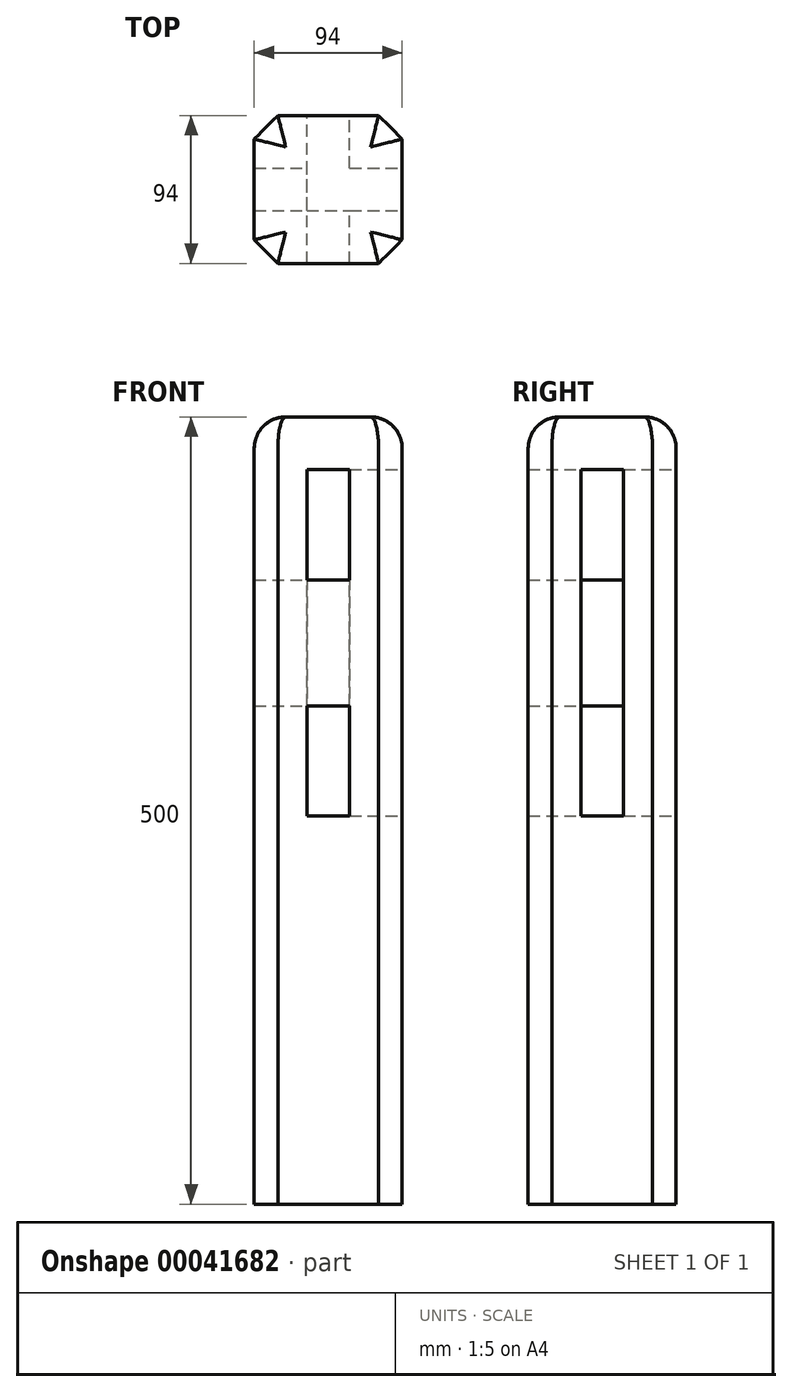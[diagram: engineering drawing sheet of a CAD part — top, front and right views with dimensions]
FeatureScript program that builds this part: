
annotation { "Feature Type Name" : "Feature", "Feature Type Description" : "" }
export const myFeature = defineFeature(function(context is Context, id is Id, definition is map)
    precondition{}
    {
        {
            var Q0;
            Q0=qCreatedBy(makeId("Top.planeOp"),FACE);
            var sketch = newSketch(context, id + "F0", { "sketchPlane" : qUnion([Q0])});
            skLineSegment(sketch, "E0.bottom", {"start": v(-47.13, 48) * mm, "end": v(46.87, 48) * mm});
            skLineSegment(sketch, "E0.top", {"start": v(-47.13, -46) * mm, "end": v(46.87, -46) * mm});
            skLineSegment(sketch, "E0.left", {"start": v(-47.13, 48) * mm, "end": v(-47.13, -46) * mm});
            skLineSegment(sketch, "E0.right", {"start": v(46.87, 48) * mm, "end": v(46.87, -46) * mm});
            skSolve(sketch);
        }
        {
            var Q0;
            Q0=makeQuery(id+"F0.imprint","IMPRINT",FACE,{"disambiguationData":[TD([[makeQuery(id+"F0.imprint","IMPRINT",EDGE,{"derivedFrom":sQuery(id+"F0.wireOp",EDGE,"E0.bottom")}),-1.0]])]});
            extrude(context, id + "F1", {"entities" : qUnion([Q0]), "depth" : 500 * mm});
        }
        {
            var Q0;
            Q0=makeQuery(id+"F1.opExtrude","SWEPT_FACE",FACE,{"disambiguationData":[OSD([sQuery(id+"F0.wireOp",EDGE,"E0.top")])]});
            var sketch = newSketch(context, id + "F2", { "sketchPlane" : qUnion([Q0])});
            skLineSegment(sketch, "E1.bottom", {"start": v(-13.63, 466.5) * mm, "end": v(13.37, 466.5) * mm});
            skLineSegment(sketch, "E1.top", {"start": v(-13.63, 246.5) * mm, "end": v(13.37, 246.5) * mm});
            skLineSegment(sketch, "E1.left", {"start": v(-13.63, 466.5) * mm, "end": v(-13.63, 246.5) * mm});
            skLineSegment(sketch, "E1.right", {"start": v(13.37, 466.5) * mm, "end": v(13.37, 246.5) * mm});
            skLineSegment(sketch, "E2.bottom", {"start": v(-13.63, 396.5) * mm, "end": v(13.37, 396.5) * mm});
            skLineSegment(sketch, "E2.top", {"start": v(-13.63, 316.5) * mm, "end": v(13.37, 316.5) * mm});
            skLineSegment(sketch, "E2.left", {"start": v(-13.63, 396.5) * mm, "end": v(-13.63, 316.5) * mm});
            skLineSegment(sketch, "E2.right", {"start": v(13.37, 396.5) * mm, "end": v(13.37, 316.5) * mm});
            skSolve(sketch);
        }
        {
            var Q0;
            Q0=qSketchRegion(id+"F2",true);
            extrude(context, id + "F3", {"entities" : qUnion([Q0]), "operationType" : NewBodyOperationType.REMOVE, "oppositeDirection" : true, "depth" : 60.5 * mm});
        }
        {
            var Q0;
            Q0=makeQuery(id+"F1.opExtrude","SWEPT_FACE",FACE,{"disambiguationData":[OSD([sQuery(id+"F0.wireOp",EDGE,"E0.right")])]});
            var sketch = newSketch(context, id + "F4", { "sketchPlane" : qUnion([Q0])});
            skLineSegment(sketch, "E3.bottom", {"start": v(-12.5, 466.5) * mm, "end": v(14.5, 466.5) * mm});
            skLineSegment(sketch, "E3.top", {"start": v(-12.5, 246.5) * mm, "end": v(14.5, 246.5) * mm});
            skLineSegment(sketch, "E3.left", {"start": v(-12.5, 466.5) * mm, "end": v(-12.5, 246.5) * mm});
            skLineSegment(sketch, "E3.right", {"start": v(14.5, 466.5) * mm, "end": v(14.5, 246.5) * mm});
            skSolve(sketch);
        }
        {
            var Q0;
            Q0=makeQuery(id+"F4.imprint","IMPRINT",FACE,{"disambiguationData":[TD([[makeQuery(id+"F4.imprint","IMPRINT",EDGE,{"derivedFrom":sQuery(id+"F4.wireOp",EDGE,"E3.bottom")}),-1.0]])]});
            extrude(context, id + "F5", {"entities" : qUnion([Q0]), "operationType" : NewBodyOperationType.REMOVE, "oppositeDirection" : true, "depth" : 60.5 * mm});
        }
        {
            var Q0;
            Q0=makeQuery(id+"F1.opExtrude","SWEPT_FACE",FACE,{"disambiguationData":[OSD([sQuery(id+"F0.wireOp",EDGE,"E0.right")])]});
            var sketch = newSketch(context, id + "F6", { "sketchPlane" : qUnion([Q0])});
            skLineSegment(sketch, "E4.bottom", {"start": v(-12.5, 396.5) * mm, "end": v(14.5, 396.5) * mm});
            skLineSegment(sketch, "E4.top", {"start": v(-12.5, 316.5) * mm, "end": v(14.5, 316.5) * mm});
            skLineSegment(sketch, "E4.left", {"start": v(-12.5, 396.5) * mm, "end": v(-12.5, 316.5) * mm});
            skLineSegment(sketch, "E4.right", {"start": v(14.5, 396.5) * mm, "end": v(14.5, 316.5) * mm});
            skSolve(sketch);
        }
        {
            var Q0;
            Q0=makeQuery(id+"F6.imprint","IMPRINT",FACE,{"disambiguationData":[TD([[makeQuery(id+"F6.imprint","IMPRINT",EDGE,{"derivedFrom":sQuery(id+"F6.wireOp",EDGE,"E4.bottom")}),-1.0]])]});
            extrude(context, id + "F7", {"entities" : qUnion([Q0]), "operationType" : NewBodyOperationType.REMOVE, "oppositeDirection" : true, "depth" : 94 * mm});
        }
        {
            var Q0;
            Q0=makeQuery(id+"F1.opExtrude","SWEPT_FACE",FACE,{"disambiguationData":[OSD([sQuery(id+"F0.wireOp",EDGE,"E0.top")])]});
            var sketch = newSketch(context, id + "F8", { "sketchPlane" : qUnion([Q0])});
            skLineSegment(sketch, "E5.bottom", {"start": v(-13.63, 466.5) * mm, "end": v(13.37, 466.5) * mm});
            skLineSegment(sketch, "E5.top", {"start": v(-13.63, 396.5) * mm, "end": v(13.37, 396.5) * mm});
            skLineSegment(sketch, "E5.left", {"start": v(-13.63, 466.5) * mm, "end": v(-13.63, 396.5) * mm});
            skLineSegment(sketch, "E5.right", {"start": v(13.37, 466.5) * mm, "end": v(13.37, 396.5) * mm});
            skLineSegment(sketch, "E6.bottom", {"start": v(-13.63, 246.5) * mm, "end": v(13.37, 246.5) * mm});
            skLineSegment(sketch, "E6.top", {"start": v(-13.63, 316.5) * mm, "end": v(13.37, 316.5) * mm});
            skLineSegment(sketch, "E6.left", {"start": v(-13.63, 246.5) * mm, "end": v(-13.63, 316.5) * mm});
            skLineSegment(sketch, "E6.right", {"start": v(13.37, 246.5) * mm, "end": v(13.37, 316.5) * mm});
            skSolve(sketch);
        }
        {
            var Q0;
            Q0=makeQuery(id+"F8.imprint","IMPRINT",FACE,{"disambiguationData":[TD([[makeQuery(id+"F8.imprint","IMPRINT",EDGE,{"derivedFrom":sQuery(id+"F8.wireOp",EDGE,"E5.bottom")}),-1.0]])]});
            var Q1;
            Q1=makeQuery(id+"F8.imprint","IMPRINT",FACE,{"disambiguationData":[TD([[makeQuery(id+"F8.imprint","IMPRINT",EDGE,{"derivedFrom":sQuery(id+"F8.wireOp",EDGE,"E6.bottom")}),1.0]])]});
            extrude(context, id + "F9", {"entities" : qUnion([Q0, Q1]), "operationType" : NewBodyOperationType.REMOVE, "oppositeDirection" : true, "depth" : 94 * mm});
        }
        {
            var Q0;
            Q0=makeQuery(id+"F1.opExtrude","SWEPT_FACE",FACE,{"disambiguationData":[OSD([sQuery(id+"F0.wireOp",EDGE,"E0.top")])]});
            cPlane(context, id + "F10", {"entities" : qUnion([Q0]), "cplaneType" : CPlaneType.OFFSET, "offset" : 150 * mm, "width" : 150 * mm, "height" : 150 * mm});
        }
        {
            var Q0;
            Q0=makeQuery(id+"F1.opExtrude","SWEPT_BODY",BODY,{"disambiguationData":[OSD([sQuery(id+"F0.wireOp",EDGE,"E0.bottom"),sQuery(id+"F0.wireOp",EDGE,"E0.top"),sQuery(id+"F0.wireOp",EDGE,"E0.left"),sQuery(id+"F0.wireOp",EDGE,"E0.right")])]});
            var Q1;
            Q1=qCreatedBy(id+"F10.planeOp",FACE);
            mirror(context, id + "F11", {"entities" : qUnion([Q0]), "mirrorPlane" : qUnion([Q1])});
        }
        {
            var Q0;
            Q0=makeQuery(id+"F11.opPattern","COPY",BODY,{"derivedFrom":makeQuery(id+"F1.opExtrude","SWEPT_BODY",BODY,{"disambiguationData":[OSD([sQuery(id+"F0.wireOp",EDGE,"E0.bottom"),sQuery(id+"F0.wireOp",EDGE,"E0.top"),sQuery(id+"F0.wireOp",EDGE,"E0.left"),sQuery(id+"F0.wireOp",EDGE,"E0.right")])]}),"instanceName":"1"});
            var Q1;
            Q1=qCreatedBy(id+"F10.planeOp",FACE);
            mirror(context, id + "F12", {"operationType" : NewBodyOperationType.REMOVE, "entities" : qUnion([Q0]), "mirrorPlane" : qUnion([Q1])});
        }
        {
            var Q0;
            Q0=makeQuery(id+"F11.opPattern","COPY",EDGE,{"derivedFrom":makeQuery(id+"F1.opExtrude","CAP_EDGE",EDGE,{"disambiguationData":[OSD([sQuery(id+"F0.wireOp",EDGE,"E0.left")])],"isStart":false}),"instanceName":"1"});
            var Q1;
            Q1=makeQuery(id+"F11.opPattern","COPY",EDGE,{"derivedFrom":makeQuery(id+"F1.opExtrude","CAP_EDGE",EDGE,{"disambiguationData":[OSD([sQuery(id+"F0.wireOp",EDGE,"E0.bottom")])],"isStart":false}),"instanceName":"1"});
            var Q2;
            Q2=makeQuery(id+"F11.opPattern","COPY",EDGE,{"derivedFrom":makeQuery(id+"F1.opExtrude","CAP_EDGE",EDGE,{"disambiguationData":[OSD([sQuery(id+"F0.wireOp",EDGE,"E0.right")])],"isStart":false}),"instanceName":"1"});
            var Q3;
            Q3=makeQuery(id+"F11.opPattern","COPY",EDGE,{"derivedFrom":makeQuery(id+"F1.opExtrude","CAP_EDGE",EDGE,{"disambiguationData":[OSD([sQuery(id+"F0.wireOp",EDGE,"E0.top")])],"isStart":false}),"instanceName":"1"});
            fillet(context, id + "F13", {"entities" : qUnion([Q0, Q1, Q2, Q3]), "radius" : 20 * mm, "tangentPropagation" : true, "allowEdgeOverflow" : false});
        }
        {
            var Q0;
            Q0=makeQuery(id+"F11.opPattern","COPY",EDGE,{"derivedFrom":makeQuery(id+"F1.opExtrude","SWEPT_EDGE",EDGE,{"disambiguationData":[OSD([sQuery(id+"F0.wireOp",EDGE,"E0.top"),sQuery(id+"F0.wireOp",EDGE,"E0.right")])]}),"instanceName":"1"});
            var Q1;
            Q1=makeQuery(id+"F11.opPattern","COPY",EDGE,{"derivedFrom":makeQuery(id+"F1.opExtrude","SWEPT_EDGE",EDGE,{"disambiguationData":[OSD([sQuery(id+"F0.wireOp",EDGE,"E0.top"),sQuery(id+"F0.wireOp",EDGE,"E0.left")])]}),"instanceName":"1"});
            var Q2;
            Q2=makeQuery(id+"F11.opPattern","COPY",EDGE,{"derivedFrom":makeQuery(id+"F1.opExtrude","SWEPT_EDGE",EDGE,{"disambiguationData":[OSD([sQuery(id+"F0.wireOp",EDGE,"E0.bottom"),sQuery(id+"F0.wireOp",EDGE,"E0.right")])]}),"instanceName":"1"});
            var Q3;
            Q3=makeQuery(id+"F11.opPattern","COPY",EDGE,{"derivedFrom":makeQuery(id+"F1.opExtrude","SWEPT_EDGE",EDGE,{"disambiguationData":[OSD([sQuery(id+"F0.wireOp",EDGE,"E0.bottom"),sQuery(id+"F0.wireOp",EDGE,"E0.left")])]}),"instanceName":"1"});
            chamfer(context, id + "F14", {"entities" : qUnion([Q0, Q1, Q2, Q3]), "width" : 15 * mm, "tangentPropagation" : true});
        }
    });
